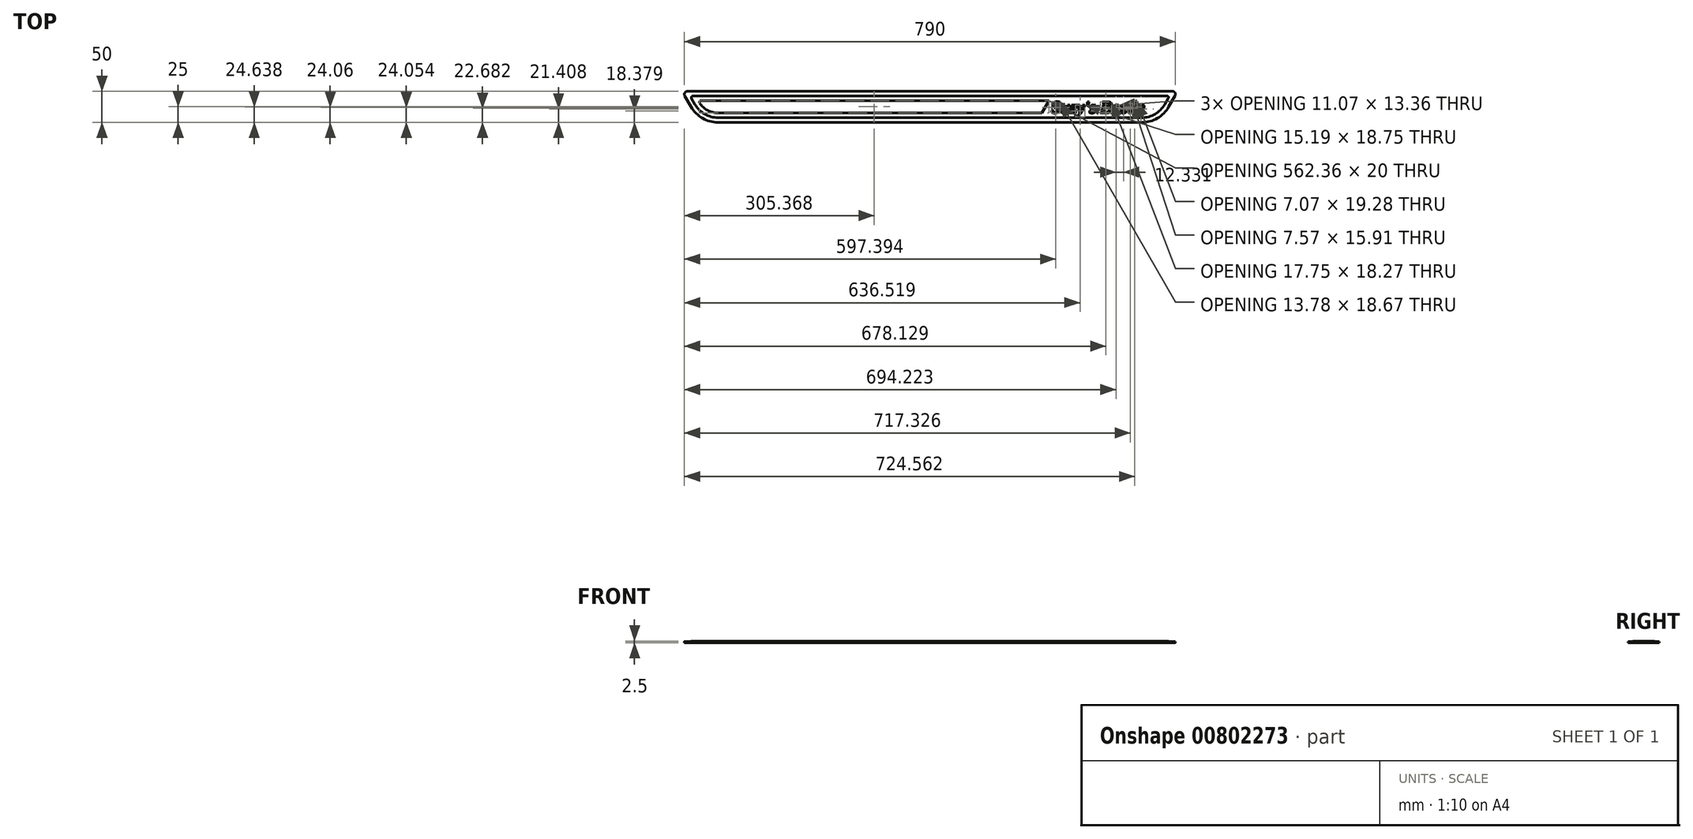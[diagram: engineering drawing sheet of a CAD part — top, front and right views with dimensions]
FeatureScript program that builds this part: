
annotation { "Feature Type Name" : "Feature", "Feature Type Description" : "" }
export const myFeature = defineFeature(function(context is Context, id is Id, definition is map)
    precondition{}
    {
        {
            var Q0;
            Q0=qCreatedBy(makeId("Top.planeOp"),FACE);
            var sketch = newSketch(context, id + "F0", { "sketchPlane" : qUnion([Q0])});
            skLineSegment(sketch, "E0.bottom", {"start": v(340.93, -25) * mm, "end": v(-340.93, -25) * mm});
            skLineSegment(sketch, "E0.top", {"start": v(390, 25) * mm, "end": v(-390, 25) * mm});
            skPoint(sketch, "E0.middle", {"position": v(0, 0) * mm});
            skLineSegment(sketch, "E1", {"start": v(-394.33, 17.5) * mm, "end": v(-384.23, 0) * mm});
            skLineSegment(sketch, "E2", {"start": v(394.33, 17.5) * mm, "end": v(384.23, 0) * mm});
            skPoint(sketch, "E3.orphan", {"position": v(-398.66, -25) * mm});
            skPoint(sketch, "E0.left.start.orphan", {"position": v(398.66, -25) * mm});
            skPoint(sketch, "E4.visualSharp", {"position": v(398.66, 25) * mm});
            skArc(sketch, "E4.filletArc", {"start": v(394.33, 17.5) * mm, "mid": v(394.33, 22.5) * mm, "end": v(390, 25) * mm});
            skPoint(sketch, "E5.visualSharp", {"position": v(-398.66, 25) * mm});
            skArc(sketch, "E5.filletArc", {"start": v(-390, 25) * mm, "mid": v(-394.33, 22.5) * mm, "end": v(-394.33, 17.5) * mm});
            skPoint(sketch, "E6.visualSharp", {"position": v(-369.8, -25) * mm});
            skArc(sketch, "E6.filletArc", {"start": v(-384.23, 0) * mm, "mid": v(-365.93, -18.3) * mm, "end": v(-340.93, -25) * mm});
            skPoint(sketch, "E7.visualSharp", {"position": v(369.8, -25) * mm});
            skArc(sketch, "E7.filletArc", {"start": v(340.93, -25) * mm, "mid": v(365.93, -18.3) * mm, "end": v(384.23, 0) * mm});
            skSolve(sketch);
        }
        {
            var Q0;
            Q0=makeQuery(id+"F0.imprint","IMPRINT",FACE,{"disambiguationData":[TD([[makeQuery(id+"F0.imprint","IMPRINT",EDGE,{"derivedFrom":sQuery(id+"F0.wireOp",EDGE,"E0.bottom")}),-1.0]])]});
            extrude(context, id + "F1", {"entities" : qUnion([Q0]), "depth" : 2 * mm, "offsetDistance" : 25 * mm});
        }
        {
            var Q0;
            Q0=makeQuery(id+"F1.opExtrude","CAP_FACE",FACE,{"disambiguationData":[OSD([sQuery(id+"F0.wireOp",EDGE,"E0.bottom"),sQuery(id+"F0.wireOp",EDGE,"E0.top"),sQuery(id+"F0.wireOp",EDGE,"E1"),sQuery(id+"F0.wireOp",EDGE,"E2"),sQuery(id+"F0.wireOp",EDGE,"E4.filletArc"),sQuery(id+"F0.wireOp",EDGE,"E5.filletArc"),sQuery(id+"F0.wireOp",EDGE,"E6.filletArc"),sQuery(id+"F0.wireOp",EDGE,"E7.filletArc")])],"isStart":false});
            var sketch = newSketch(context, id + "F2", { "sketchPlane" : qUnion([Q0])});
            skLineSegment(sketch, "E8.0", {"start": v(377.73, 3.75) * mm, "end": v(383.5, 13.75) * mm});
            skLineSegment(sketch, "E8.1", {"start": v(-383.5, 13.75) * mm, "end": v(-377.73, 3.75) * mm});
            skArc(sketch, "E8.2", {"start": v(-377.73, 3.75) * mm, "mid": v(-362.18, -11.8) * mm, "end": v(-340.93, -17.5) * mm});
            skLineSegment(sketch, "E8.3", {"start": v(381.34, 17.5) * mm, "end": v(-381.34, 17.5) * mm});
            skLineSegment(sketch, "E8.4", {"start": v(-340.93, -17.5) * mm, "end": v(340.93, -17.5) * mm});
            skArc(sketch, "E8.5", {"start": v(340.93, -17.5) * mm, "mid": v(362.18, -11.8) * mm, "end": v(377.73, 3.75) * mm});
            skPoint(sketch, "E9.visualSharp", {"position": v(-385.67, 17.5) * mm});
            skArc(sketch, "E9.filletArc", {"start": v(-381.34, 17.5) * mm, "mid": v(-383.5, 16.25) * mm, "end": v(-383.5, 13.75) * mm});
            skPoint(sketch, "E10.visualSharp", {"position": v(385.67, 17.5) * mm});
            skArc(sketch, "E10.filletArc", {"start": v(383.5, 13.75) * mm, "mid": v(383.5, 16.25) * mm, "end": v(381.34, 17.5) * mm});
            skLineSegment(sketch, "E11.0", {"start": v(191.55, 10) * mm, "end": v(-368.31, 10) * mm});
            skLineSegment(sketch, "E11.2", {"start": v(-340.93, -10) * mm, "end": v(180, -10) * mm});
            skPoint(sketch, "E12.0.2.start.orphan", {"position": v(-390, 25) * mm});
            skPoint(sketch, "E12.0.3.start.orphan", {"position": v(-394.33, 17.5) * mm});
            skPoint(sketch, "E12.0.4.start.orphan", {"position": v(-384.23, 0) * mm});
            skPoint(sketch, "E12.0.5.start.orphan", {"position": v(-340.93, -25) * mm});
            skPoint(sketch, "E12.0.0.end.orphan", {"position": v(390, 25) * mm});
            skPoint(sketch, "E12.0.7.end.orphan", {"position": v(394.33, 17.5) * mm});
            skPoint(sketch, "E12.0.6.end.orphan", {"position": v(384.23, 0) * mm});
            skPoint(sketch, "E12.0.6.start.orphan", {"position": v(340.93, -25) * mm});
            skPoint(sketch, "E13.visualSharp", {"position": v(372.55, 10) * mm});
            skLineSegment(sketch, "E14.MirrorCS", {"start": v(191.55, 10) * mm, "end": v(180, -10) * mm});
            skArc(sketch, "E15.MirrorCS", {"start": v(-340.93, -10) * mm, "mid": v(-357.74, -5.7) * mm, "end": v(-370.42, 6.15) * mm});
            skArc(sketch, "E16.MirrorCS", {"start": v(-370.42, 6.15) * mm, "mid": v(-370.5, 8.7) * mm, "end": v(-368.31, 10) * mm});
            skPoint(sketch, "E11.1.start.orphan", {"position": v(340.93, -10) * mm});
            skPoint(sketch, "E13.filletArc.end.orphan", {"position": v(368.31, 10) * mm});
            skPoint(sketch, "E13.filletArc.start.orphan", {"position": v(370.42, 6.15) * mm});
            skSolve(sketch);
        }
        {
            var Q0;
            Q0 = qSketchRegion(id + "F2", true);
            extrude(context, id + "F3", {"entities" : qUnion([Q0]), "depth" : .5 * mm, "offsetDistance" : 25 * mm});
        }
        {
            var Q0;
            Q0=makeQuery(id+"F3.opExtrude","CAP_FACE",FACE,{"disambiguationData":[OSD([sQuery(id+"F2.wireOp",EDGE,"E8.0"),sQuery(id+"F2.wireOp",EDGE,"E8.1"),sQuery(id+"F2.wireOp",EDGE,"E8.2"),sQuery(id+"F2.wireOp",EDGE,"E8.3"),sQuery(id+"F2.wireOp",EDGE,"E8.4"),sQuery(id+"F2.wireOp",EDGE,"E8.5"),sQuery(id+"F2.wireOp",EDGE,"E9.filletArc"),sQuery(id+"F2.wireOp",EDGE,"E10.filletArc"),sQuery(id+"F2.wireOp",EDGE,"E11.0"),sQuery(id+"F2.wireOp",EDGE,"E11.1"),sQuery(id+"F2.wireOp",EDGE,"E11.2"),sQuery(id+"F2.wireOp",EDGE,"MTWN2MBK-J4X0-sjEC-n86w-c7D5PN64avD3"),sQuery(id+"F2.wireOp",EDGE,"E13.filletArc")])],"isStart":false});
            var sketch = newSketch(context, id + "F4", { "sketchPlane" : qUnion([Q0])});
            skText(sketch, "E17", { "text": "Suzy\'s Beetle", "fontName": "Tinos-BoldItalic.ttf"});
            const initialGuessF4  = {"E17": [0.195, -0.01, 1, 0, 0.02]};
            skSetInitialGuess(sketch, initialGuessF4);
            skSolve(sketch);
        }
        {
            var Q0;
            Q0 = qSketchRegion(id + "F4", true);
            extrude(context, id + "F5", {"entities" : qUnion([Q0]), "operationType" : NewBodyOperationType.REMOVE, "oppositeDirection" : true, "depth" : .5 * mm, "offsetDistance" : 25 * mm});
        }
    });
